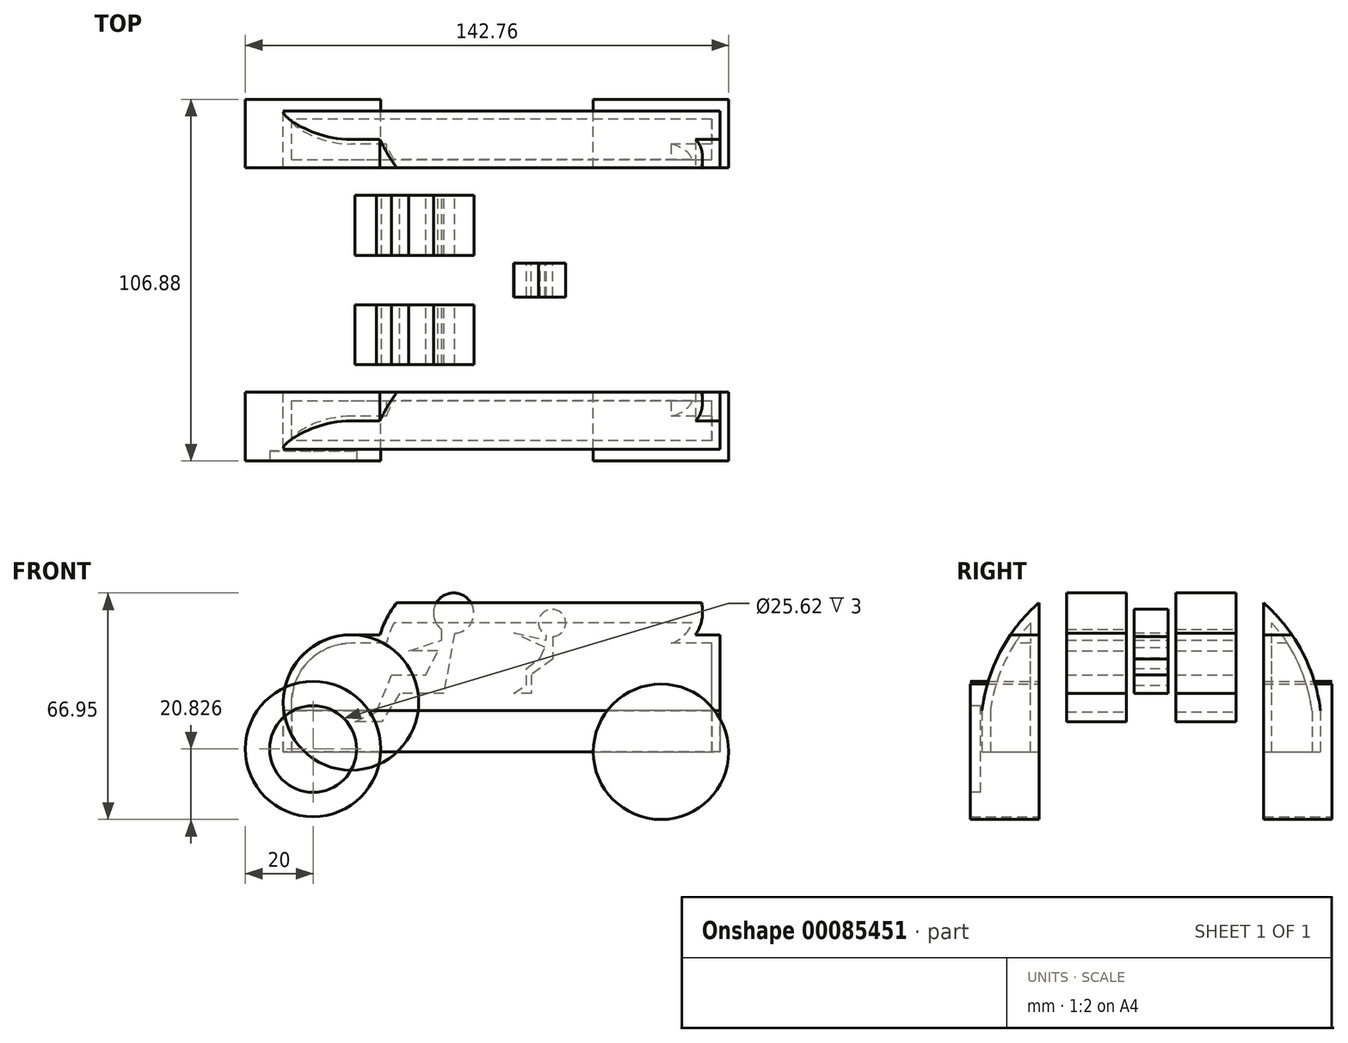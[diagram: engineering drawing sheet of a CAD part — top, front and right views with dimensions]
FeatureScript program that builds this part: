
annotation { "Feature Type Name" : "Feature", "Feature Type Description" : "" }
export const myFeature = defineFeature(function(context is Context, id is Id, definition is map)
    precondition{}
    {
        {
            var Q0;
            Q0=qCreatedBy(makeId("Front.planeOp"),FACE);
            var sketch = newSketch(context, id + "F0", { "sketchPlane" : qUnion([Q0])});
            skLineSegment(sketch, "E0.bottom", {"start": v(64.51, 17.27) * mm, "end": v(-64.51, 17.27) * mm});
            skLineSegment(sketch, "E0.top", {"start": v(64.51, -17.27) * mm, "end": v(-64.51, -17.27) * mm});
            skLineSegment(sketch, "E0.left", {"start": v(64.51, 17.27) * mm, "end": v(64.51, -17.27) * mm});
            skLineSegment(sketch, "E0.right", {"start": v(-64.51, 17.27) * mm, "end": v(-64.51, -17.27) * mm});
            skPoint(sketch, "E0.middle", {"position": v(0, 0) * mm});
            skSolve(sketch);
        }
        {
            var Q0;
            Q0 = qSketchRegion(id + "F0", true);
            extrude(context, id + "F1", {"entities" : qUnion([Q0]), "endBound" : BoundingType.SYMMETRIC, "depth" : 100 * mm});
        }
        {
            var Q0;
            Q0=makeQuery(id+"F1.opExtrude","CAP_FACE",FACE,{"disambiguationData":[OSD([sQuery(id+"F0.wireOp",EDGE,"E0.bottom"),sQuery(id+"F0.wireOp",EDGE,"E0.top"),sQuery(id+"F0.wireOp",EDGE,"E0.left"),sQuery(id+"F0.wireOp",EDGE,"E0.right")])],"isStart":false});
            var sketch = newSketch(context, id + "F2", { "sketchPlane" : qUnion([Q0])});
            skArc(sketch, "E1", {"start": v(-18.12, 36.36) * mm, "mid": v(-29.23, 28.86) * mm, "end": v(-35.97, 17.27) * mm});
            skLineSegment(sketch, "E2", {"start": v(-18.12, 36.36) * mm, "end": v(47.03, 36.36) * mm});
            skArc(sketch, "E3", {"start": v(57.24, 17.27) * mm, "mid": v(57.85, 29.87) * mm, "end": v(47.03, 36.36) * mm});
            skLineSegment(sketch, "E4.0", {"start": v(64.51, 17.27) * mm, "end": v(-64.51, 17.27) * mm});
            skSolve(sketch);
        }
        {
            var Q0;
            Q0 = qSketchRegion(id + "F2", true);
            extrude(context, id + "F3", {"entities" : qUnion([Q0]), "operationType" : NewBodyOperationType.ADD, "oppositeDirection" : true, "depth" : 100.07 * mm});
        }
        {
            var Q0;
            Q0=makeQuery(id+"F1.opExtrude","SWEPT_FACE",FACE,{"disambiguationData":[OSD([sQuery(id+"F0.wireOp",EDGE,"E0.right")])]});
            var sketch = newSketch(context, id + "F4", { "sketchPlane" : qUnion([Q0])});
            skArc(sketch, "E5", {"start": v(50, -17.27) * mm, "mid": v(0, 39.2) * mm, "end": v(-50, -17.27) * mm});
            skLineSegment(sketch, "E6.0", {"start": v(50, -17.27) * mm, "end": v(-50, -17.27) * mm});
            skLineSegment(sketch, "E7.bottom", {"start": v(-59.48, 45.07) * mm, "end": v(65.36, 45.07) * mm});
            skLineSegment(sketch, "E7.top", {"start": v(-59.48, -31.35) * mm, "end": v(65.36, -31.35) * mm});
            skLineSegment(sketch, "E7.left", {"start": v(-59.48, 45.07) * mm, "end": v(-59.48, -31.35) * mm});
            skLineSegment(sketch, "E7.right", {"start": v(65.36, 45.07) * mm, "end": v(65.36, -31.35) * mm});
            skSolve(sketch);
        }
        {
            var Q0;
            Q0 = qSketchRegion(id + "F4", true);
            extrude(context, id + "F5", {"entities" : qUnion([Q0]), "operationType" : NewBodyOperationType.REMOVE, "endBound" : BoundingType.THROUGH_ALL, "oppositeDirection" : true, "depth" : 25 * mm});
        }
        {
            var Q0;
            Q0=qCreatedBy(makeId("Front.planeOp"),FACE);
            var sketch = newSketch(context, id + "F6", { "sketchPlane" : qUnion([Q0])});
            skCircle(sketch, "E8", {"center": v(-55.72, -16.47) * mm, "radius": 20 * mm});
            skCircle(sketch, "E9", {"center": v(47.04, -17.3) * mm, "radius": 20 * mm});
            skSolve(sketch);
        }
        {
            var Q0;
            Q0 = qSketchRegion(id + "F6", true);
            extrude(context, id + "F7", {"entities" : qUnion([Q0]), "endBound" : BoundingType.SYMMETRIC, "depth" : 106.88 * mm});
        }
        {
            var Q0;
            Q0=qCreatedBy(makeId("Right.planeOp"),FACE);
            var sketch = newSketch(context, id + "F8", { "sketchPlane" : qUnion([Q0])});
            skLineSegment(sketch, "E10.bottom", {"start": v(-33.15, -45.3) * mm, "end": v(33.15, -45.3) * mm});
            skLineSegment(sketch, "E10.top", {"start": v(-33.15, 45.3) * mm, "end": v(33.15, 45.3) * mm});
            skLineSegment(sketch, "E10.left", {"start": v(-33.15, -45.3) * mm, "end": v(-33.15, 45.3) * mm});
            skLineSegment(sketch, "E10.right", {"start": v(33.15, -45.3) * mm, "end": v(33.15, 45.3) * mm});
            skPoint(sketch, "E10.middle", {"position": v(0, 0) * mm});
            skSolve(sketch);
        }
        {
            var Q0;
            Q0 = qSketchRegion(id + "F8", true);
            extrude(context, id + "F9", {"entities" : qUnion([Q0]), "operationType" : NewBodyOperationType.REMOVE, "endBound" : BoundingType.THROUGH_ALL, "oppositeDirection" : true, "depth" : 25 * mm, "hasSecondDirection" : true, "secondDirectionBound" : SecondDirectionBoundingType.THROUGH_ALL, "secondDirectionOppositeDirection" : false, "secondDirectionDepth" : 25 * mm});
        }
        {
            var Q0;
            Q0=makeQuery(id+"F1.opExtrude","SWEPT_EDGE",EDGE,{"disambiguationData":[OSD([sQuery(id+"F0.wireOp",EDGE,"E0.bottom"),sQuery(id+"F0.wireOp",EDGE,"E0.right")])]});
            fillet(context, id + "F10", {"entities" : qUnion([Q0]), "radius" : 20 * mm, "tangentPropagation" : true, "allowEdgeOverflow" : false});
        }
        {
            var Q0;
            Q0=makeQuery(id+"F1.opExtrude","SWEPT_FACE",FACE,{"disambiguationData":[OSD([sQuery(id+"F0.wireOp",EDGE,"E0.top")])]});
            shell(context, id + "F11", {"entities" : qUnion([Q0]), "thickness" : 2.5 * mm});
        }
        {
            var Q0;
            Q0=qCreatedBy(makeId("Front.planeOp"),FACE);
            var sketch = newSketch(context, id + "F12", { "sketchPlane" : qUnion([Q0])});
            skArc(sketch, "E11", {"start": v(-13.94, 17.73) * mm, "mid": v(-12.52, 29.4) * mm, "end": v(-17.65, 18.82) * mm});
            skLineSegment(sketch, "E12", {"start": v(-13.94, 17.73) * mm, "end": v(-17.12, 0) * mm});
            skLineSegment(sketch, "E13", {"start": v(-17.12, 0) * mm, "end": v(-30.12, 0) * mm});
            skLineSegment(sketch, "E14", {"start": v(-30.12, 0) * mm, "end": v(-35.42, -8.4) * mm});
            skLineSegment(sketch, "E15", {"start": v(-35.42, -8.4) * mm, "end": v(-43.38, -8.4) * mm});
            skLineSegment(sketch, "E16", {"start": v(-43.38, -8.4) * mm, "end": v(-37.01, -5.49) * mm});
            skLineSegment(sketch, "E17", {"start": v(-37.01, -5.49) * mm, "end": v(-32.5, 5.39) * mm});
            skLineSegment(sketch, "E18", {"start": v(-32.5, 5.39) * mm, "end": v(-22.42, 5.39) * mm});
            skLineSegment(sketch, "E19", {"start": v(-22.42, 5.39) * mm, "end": v(-18.84, 12.55) * mm});
            skLineSegment(sketch, "E20", {"start": v(-18.84, 12.55) * mm, "end": v(-27.46, 12.55) * mm});
            skPoint(sketch, "E20.endSnap0", {"position": v(-27.46, 5.39) * mm});
            skLineSegment(sketch, "E21", {"start": v(-27.46, 12.55) * mm, "end": v(-17.65, 15.73) * mm});
            skLineSegment(sketch, "E22", {"start": v(-17.65, 15.73) * mm, "end": v(-17.65, 18.82) * mm});
            skSolve(sketch);
        }
        {
            var Q0;
            Q0 = qSketchRegion(id + "F12", true);
            extrude(context, id + "F13", {"entities" : qUnion([Q0]), "depth" : 25 * mm, "hasSecondDirection" : true, "secondDirectionOppositeDirection" : true, "secondDirectionDepth" : 25 * mm});
        }
        {
            var Q0;
            Q0=qCreatedBy(makeId("Right.planeOp"),FACE);
            var sketch = newSketch(context, id + "F14", { "sketchPlane" : qUnion([Q0])});
            skLineSegment(sketch, "E23.bottom", {"start": v(-7.3, -19.26) * mm, "end": v(7.3, -19.26) * mm});
            skLineSegment(sketch, "E23.top", {"start": v(-7.3, 38.97) * mm, "end": v(7.3, 38.97) * mm});
            skLineSegment(sketch, "E23.left", {"start": v(-7.3, -19.26) * mm, "end": v(-7.3, 38.97) * mm});
            skLineSegment(sketch, "E23.right", {"start": v(7.3, -19.26) * mm, "end": v(7.3, 38.97) * mm});
            skPoint(sketch, "E23.middle", {"position": v(0, 9.86) * mm});
            skSolve(sketch);
        }
        {
            var Q0;
            Q0 = qSketchRegion(id + "F14", true);
            extrude(context, id + "F15", {"entities" : qUnion([Q0]), "operationType" : NewBodyOperationType.REMOVE, "endBound" : BoundingType.THROUGH_ALL, "depth" : 25 * mm, "hasSecondDirection" : true, "secondDirectionBound" : SecondDirectionBoundingType.THROUGH_ALL, "secondDirectionOppositeDirection" : true, "secondDirectionDepth" : 25 * mm});
        }
        {
            var Q0;
            Q0=qCreatedBy(makeId("Front.planeOp"),FACE);
            var sketch = newSketch(context, id + "F16", { "sketchPlane" : qUnion([Q0])});
            skArc(sketch, "E24", {"start": v(15.07, 16.77) * mm, "mid": v(15.65, 24.72) * mm, "end": v(13.14, 17.15) * mm});
            skLineSegment(sketch, "E25", {"start": v(15.07, 16.77) * mm, "end": v(15.07, 10.17) * mm});
            skLineSegment(sketch, "E26", {"start": v(15.07, 10.17) * mm, "end": v(8.73, 5.45) * mm});
            skLineSegment(sketch, "E27", {"start": v(8.73, 5.45) * mm, "end": v(8.73, 0) * mm});
            skLineSegment(sketch, "E28", {"start": v(8.73, 0) * mm, "end": v(3.54, 0) * mm});
            skLineSegment(sketch, "E29", {"start": v(3.54, 0) * mm, "end": v(7.25, 2.33) * mm});
            skLineSegment(sketch, "E30", {"start": v(7.25, 2.33) * mm, "end": v(7.25, 7.29) * mm});
            skLineSegment(sketch, "E31", {"start": v(7.25, 7.29) * mm, "end": v(11.36, 10.56) * mm});
            skLineSegment(sketch, "E32", {"start": v(11.36, 10.56) * mm, "end": v(12.76, 13.54) * mm});
            skLineSegment(sketch, "E33", {"start": v(12.76, 13.54) * mm, "end": v(3.59, 17.85) * mm});
            skLineSegment(sketch, "E34", {"start": v(3.59, 17.85) * mm, "end": v(13.14, 15.7) * mm});
            skLineSegment(sketch, "E35", {"start": v(13.14, 15.7) * mm, "end": v(13.14, 17.15) * mm});
            skSolve(sketch);
        }
        {
            var Q0;
            Q0 = qSketchRegion(id + "F16", true);
            extrude(context, id + "F17", {"entities" : qUnion([Q0]), "endBound" : BoundingType.SYMMETRIC, "depth" : 10 * mm});
        }
        {
            var Q0;
            Q0=makeQuery(id+"F7.opExtrude","CAP_FACE",FACE,{"disambiguationData":[OSD([sQuery(id+"F6.wireOp",EDGE,"E8")])],"isStart":false});
            var sketch = newSketch(context, id + "F18", { "sketchPlane" : qUnion([Q0])});
            skCircle(sketch, "E36", {"center": v(-55.72, -16.47) * mm, "radius": 12.81 * mm});
            skSolve(sketch);
        }
        {
            var Q0;
            Q0 = qSketchRegion(id + "F18", true);
            extrude(context, id + "F19", {"entities" : qUnion([Q0]), "operationType" : NewBodyOperationType.REMOVE, "oppositeDirection" : true, "depth" : 3 * mm});
        }
    });
